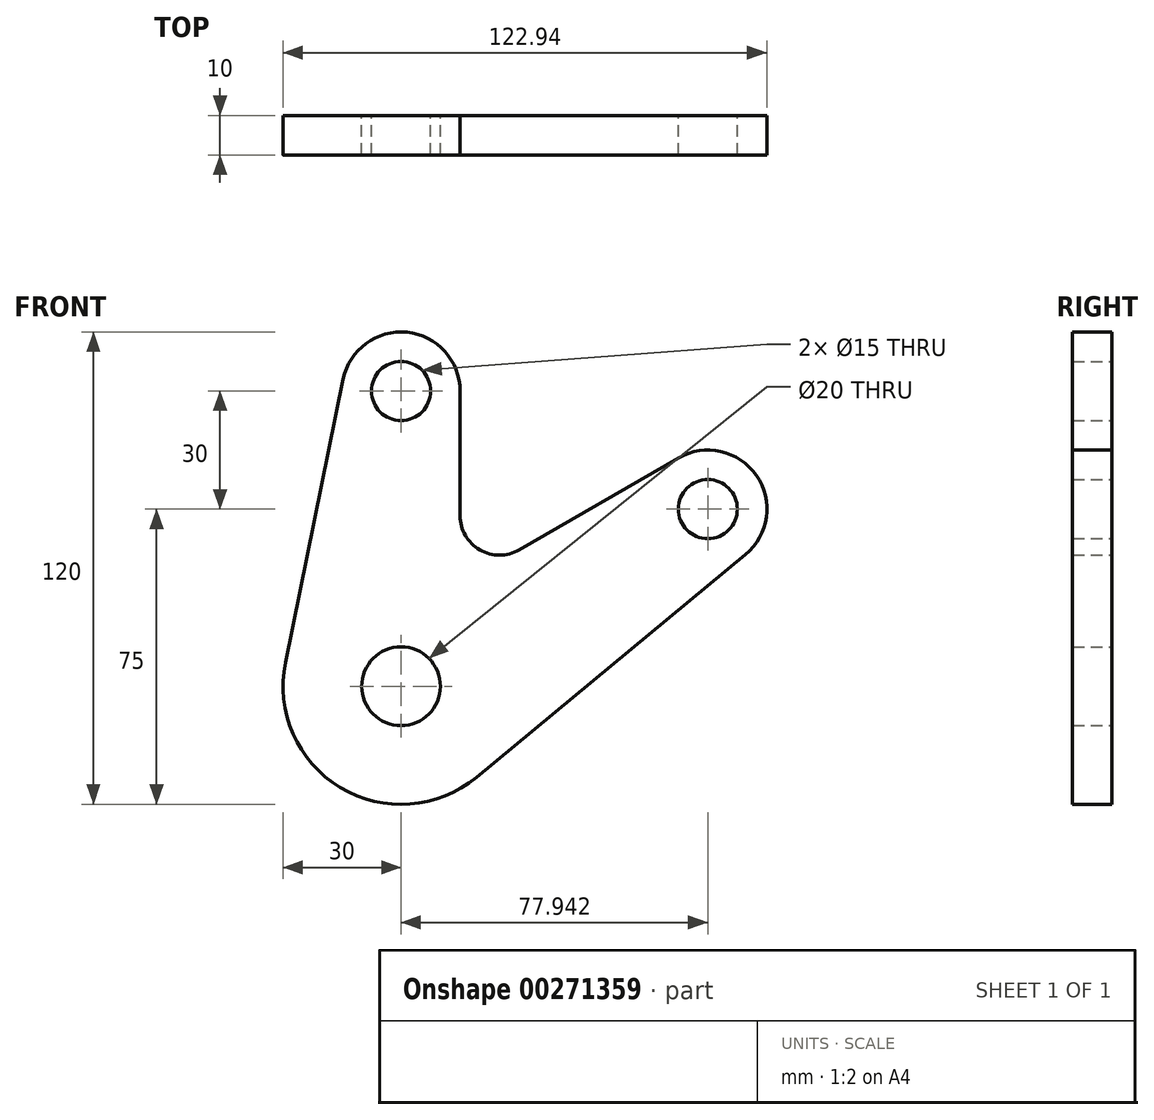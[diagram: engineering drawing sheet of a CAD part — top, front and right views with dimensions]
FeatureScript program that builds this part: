
annotation { "Feature Type Name" : "Feature", "Feature Type Description" : "" }
export const myFeature = defineFeature(function(context is Context, id is Id, definition is map)
    precondition{}
    {
        {
            var Q0;
            Q0=qCreatedBy(makeId("Front.planeOp"),FACE);
            var sketch = newSketch(context, id + "F0", { "sketchPlane" : qUnion([Q0])});
            skCircle(sketch, "E0", {"center": v(0, 0) * mm, "radius": 10 * mm});
            skCircle(sketch, "E1", {"center": v(0, 75) * mm, "radius": 7.5 * mm});
            skLineSegment(sketch, "E2", {"start": v(0, 0) * mm, "end": v(77.94, 45) * mm, "construction": true});
            skLineSegment(sketch, "E3", {"start": v(0, 0) * mm, "end": v(0, 75) * mm, "construction": true});
            skCircle(sketch, "E4", {"center": v(77.94, 45) * mm, "radius": 7.5 * mm});
            skArc(sketch, "E5", {"start": v(-29.4, 6) * mm, "mid": v(-15.44, -25.72) * mm, "end": v(19.12, -23.12) * mm});
            skArc(sketch, "E6", {"start": v(-14.7, 78) * mm, "mid": v(1.5, 89.92) * mm, "end": v(15, 75) * mm});
            skLineSegment(sketch, "E7", {"start": v(15, 75) * mm, "end": v(15, 43.3) * mm});
            skArc(sketch, "E8", {"start": v(70.44, 58) * mm, "mid": v(90.26, 53.56) * mm, "end": v(87.5, 33.44) * mm});
            skLineSegment(sketch, "E9", {"start": v(87.5, 33.44) * mm, "end": v(19.12, -23.12) * mm});
            skLineSegment(sketch, "E10", {"start": v(-14.7, 78) * mm, "end": v(-29.4, 6) * mm});
            skLineSegment(sketch, "E11", {"start": v(70.44, 58) * mm, "end": v(30, 34.64) * mm});
            skArc(sketch, "E12", {"start": v(15, 43.3) * mm, "mid": v(20, 34.64) * mm, "end": v(30, 34.64) * mm});
            skSolve(sketch);
        }
        {
            var Q0;
            Q0 = qSketchRegion(id + "F0", true);
            extrude(context, id + "F1", {"entities" : qUnion([Q0]), "depth" : 10 * mm});
        }
    });
